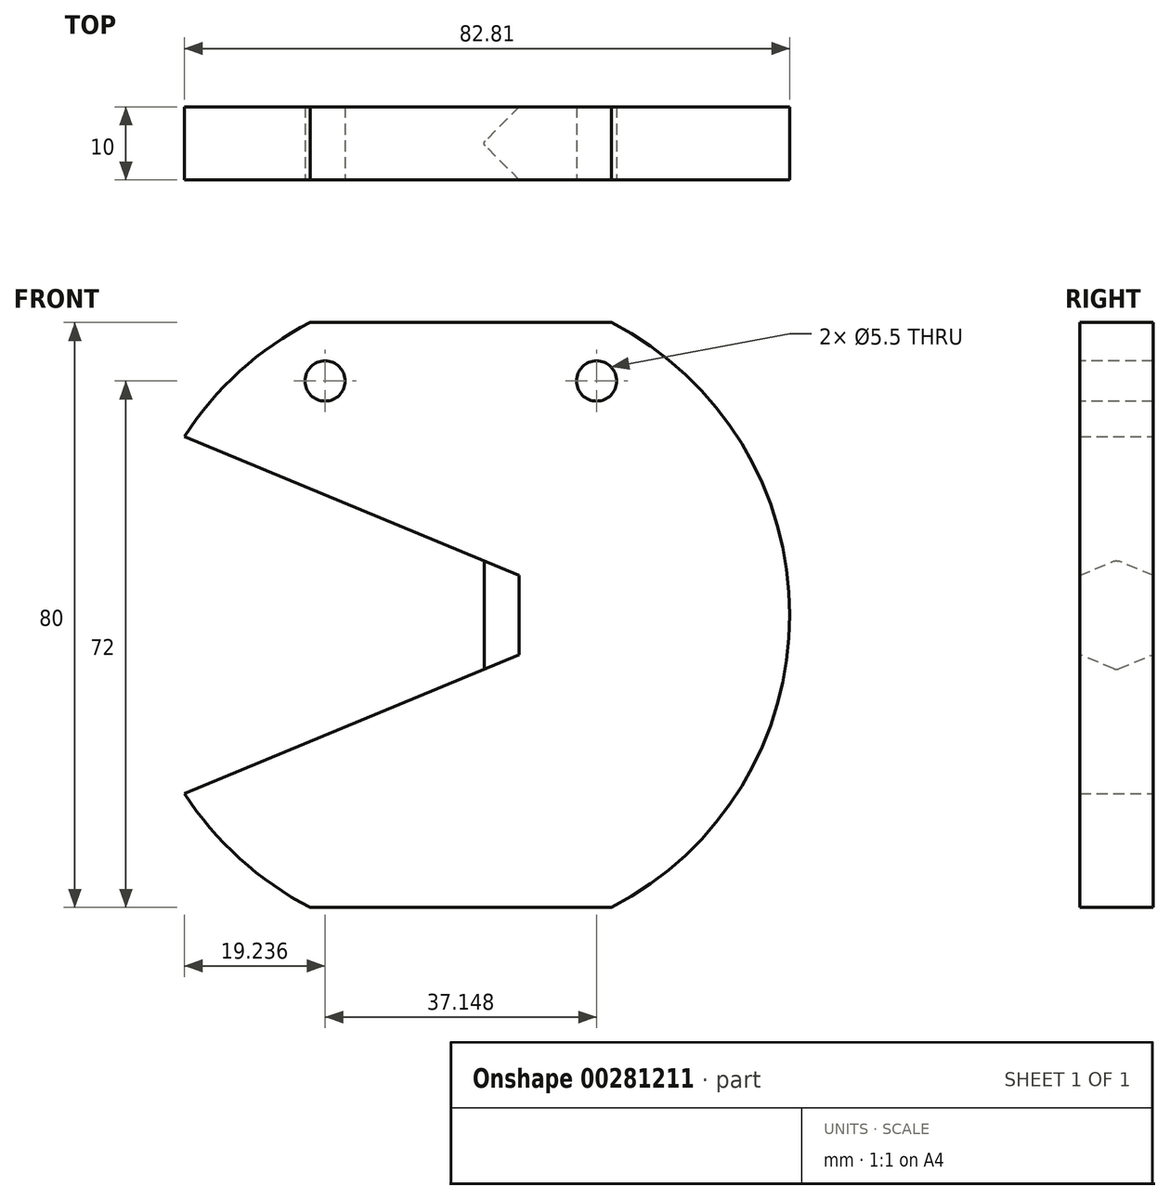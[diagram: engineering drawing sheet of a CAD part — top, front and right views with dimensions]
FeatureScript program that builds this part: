
annotation { "Feature Type Name" : "Feature", "Feature Type Description" : "" }
export const myFeature = defineFeature(function(context is Context, id is Id, definition is map)
    precondition{}
    {
        {
            var Q0;
            Q0=qCreatedBy(makeId("Front.planeOp"),FACE);
            var sketch = newSketch(context, id + "F0", { "sketchPlane" : qUnion([Q0])});
            skLineSegment(sketch, "E0", {"start": v(0, -7.5) * mm, "end": v(0, 7.5) * mm});
            skPoint(sketch, "E1", {"position": v(0, 0) * mm});
            skArc(sketch, "E2", {"start": v(-40.8, -24.4) * mm, "mid": v(42, 0) * mm, "end": v(-40.8, 24.4) * mm});
            skLineSegment(sketch, "E3", {"start": v(0, 7.5) * mm, "end": v(-40.8, 24.4) * mm});
            skLineSegment(sketch, "E4", {"start": v(0, 0) * mm, "end": v(-46.33, 0) * mm, "construction": true});
            skLineSegment(sketch, "E5.MirrorCS", {"start": v(0, -7.5) * mm, "end": v(-40.8, -24.4) * mm});
            skArc(sketch, "E6.MirrorC", {"start": v(-40.8, 24.4) * mm, "mid": v(42, 0) * mm, "end": v(-40.8, -24.4) * mm});
            skCircle(sketch, "E7", {"center": v(-4.66, 27.17) * mm, "radius": 4.43 * mm});
            skLineSegment(sketch, "E8.bottom", {"start": v(-70.5, 40) * mm, "end": v(72.68, 40) * mm});
            skLineSegment(sketch, "E8.top", {"start": v(-70.5, -40) * mm, "end": v(72.68, -40) * mm});
            skLineSegment(sketch, "E8.left", {"start": v(-70.5, 40) * mm, "end": v(-70.5, -40) * mm});
            skLineSegment(sketch, "E8.right", {"start": v(72.68, 40) * mm, "end": v(72.68, -40) * mm});
            skPoint(sketch, "E8.middle", {"position": v(1.1, 0) * mm});
            skSolve(sketch);
        }
        {
            var Q0;
            Q0=makeQuery(id+"F0.imprint","IMPRINT",FACE,{"disambiguationData":[TD([[makeQuery(id+"F0.imprint","IMPRINT",EDGE,{"derivedFrom":sQuery(id+"F0.wireOp",EDGE,"E0")}),-1.0]])]});
            var Q1;
            Q1=makeQuery(id+"F0.imprint","IMPRINT",FACE,{"disambiguationData":[TD([[makeQuery(id+"F0.imprint","IMPRINT",EDGE,{"derivedFrom":sQuery(id+"F0.wireOp",EDGE,"E7")}),1.0]])]});
            extrude(context, id + "F1", {"entities" : qUnion([Q0, Q1]), "endBound" : BoundingType.SYMMETRIC, "depth" : 10 * mm, "offsetDistance" : 25 * mm});
        }
        {
            var Q0;
            Q0=makeQuery(id+"F1.opExtrude","CAP_FACE",FACE,{"disambiguationData":[OSD([sQuery(id+"F0.wireOp",EDGE,"E0"),sQuery(id+"F0.wireOp",EDGE,"E5.MirrorCS"),sQuery(id+"F0.wireOp",EDGE,"E6.MirrorC"),sQuery(id+"F0.wireOp",EDGE,"E3"),sQuery(id+"F0.wireOp",EDGE,"E8.bottom"),sQuery(id+"F0.wireOp",EDGE,"E8.top")])],"isStart":false});
            var sketch = newSketch(context, id + "F2", { "sketchPlane" : qUnion([Q0])});
            skCircle(sketch, "E9", {"center": v(-3, 0) * mm, "radius": 37 * mm, "construction": true});
            skLineSegment(sketch, "E10", {"start": v(-34.64, 32) * mm, "end": v(28.64, 32) * mm, "construction": true});
            skPoint(sketch, "E11", {"position": v(-21.57, 32) * mm});
            skPoint(sketch, "E12", {"position": v(15.57, 32) * mm});
            skSolve(sketch);
        }
        {
            var Q0;
            Q0=sQuery(id+"F2.wireOp",VERTEX,"E11");
            var Q1;
            Q1=sQuery(id+"F2.wireOp",VERTEX,"E12");
            var Q2;
            Q2=makeQuery(id+"F1.opExtrude","SWEPT_BODY",BODY,{"disambiguationData":[OSD([sQuery(id+"F0.wireOp",EDGE,"E0"),sQuery(id+"F0.wireOp",EDGE,"E5.MirrorCS"),sQuery(id+"F0.wireOp",EDGE,"E6.MirrorC"),sQuery(id+"F0.wireOp",EDGE,"E3"),sQuery(id+"F0.wireOp",EDGE,"E8.bottom"),sQuery(id+"F0.wireOp",EDGE,"E8.top")])]});
            hole(context, id + "F3", {"style" : HoleStyle.SIMPLE, "endStyle" : HoleEndStyle.THROUGH, "standardTappedOrClearance" : lookupTablePath({ "standard" : "ISO", "fit" : "Normal", "size" : "M5", "type" : "Clearance" }), "standardBlindInLast" : lookupTablePath({ "fit" : "Standard", "standard" : "ISO", "size" : "M5", "type" : "Clearance" }), "holeDiameter" : 5.5 * mm, "majorDiameter" : 5 * mm, "isTappedThrough" : true, "tappedDepth" : 12 * mm, "tapClearance" : 3, "locations" : qUnion([Q0, Q1]), "scope" : qUnion([Q2])});
        }
        {
            var Q0;
            Q0=makeQuery(id+"F1.opExtrude","CAP_EDGE",EDGE,{"disambiguationData":[OSD([sQuery(id+"F0.wireOp",EDGE,"E0")])],"isStart":false});
            var Q1;
            Q1=makeQuery(id+"F1.opExtrude","CAP_EDGE",EDGE,{"disambiguationData":[OSD([sQuery(id+"F0.wireOp",EDGE,"E0")])],"isStart":true});
            chamfer(context, id + "F4", {"entities" : qUnion([Q0, Q1]), "width" : 5 * mm, "tangentPropagation" : true});
        }
        {
            var Q0;
            {var subQ0=sQuery(id+"F0.wireOp",EDGE,"E0");Q0=makeQuery(id+"F4.opChamfer","BLEND_EDGE",EDGE,{"blendedFrom":[makeQuery(id+"F1.opExtrude","CAP_EDGE",EDGE,{"disambiguationData":[OSD([subQ0])],"isStart":true}),makeQuery(id+"F1.opExtrude","CAP_EDGE",EDGE,{"disambiguationData":[OSD([subQ0])],"isStart":false})],"blendedInto":[]});}
            fillet(context, id + "F5", {"entities" : qUnion([Q0]), "radius" : 0.5 * mm, "tangentPropagation" : true, "allowEdgeOverflow" : false});
        }
    });
